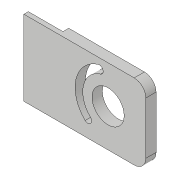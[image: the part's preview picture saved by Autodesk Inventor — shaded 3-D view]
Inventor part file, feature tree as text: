
AUTODESK INVENTOR PART (.ipt)
format: ipt  version: 2018.3 (Build 223284000, 284)  size: 130,048 bytes
history: native  units: in
note: dims shown in document units (in); Inventor stores cm internally (conversion verified against a paired STEP export)
features: extrude x2, sketch x2, fillet x1
ambient origin geometry x8: Origin, YZ Plane, XZ Plane, XY Plane, X Axis, Y Axis, Z Axis, Center Point
bodies: Solid1 (feature_tree)
feature tree (5):
  extrude  "Extrusion1"  Depth=0.221in TaperAngle=0.0deg
  extrude  "Extrusion5"  Depth=0.082in
  fillet  "Fillet1"  Radius=1.25in
  sketch  "Sketch1"  dims[d0=1.625in d1=2.625in d4=0.6925in d5=0.8125in d8=0.221in d9=0.0in]
  sketch  "Sketch5"  dims[d22=0.8125in d23=1.0in d24=1.25in d37=0.119in d38=0.625in d39=0.125in d40=0.125in d41=0.0in d42=0.25in d43=0.0625in d44=0.085in d54=0.082in d55=0.628in]
